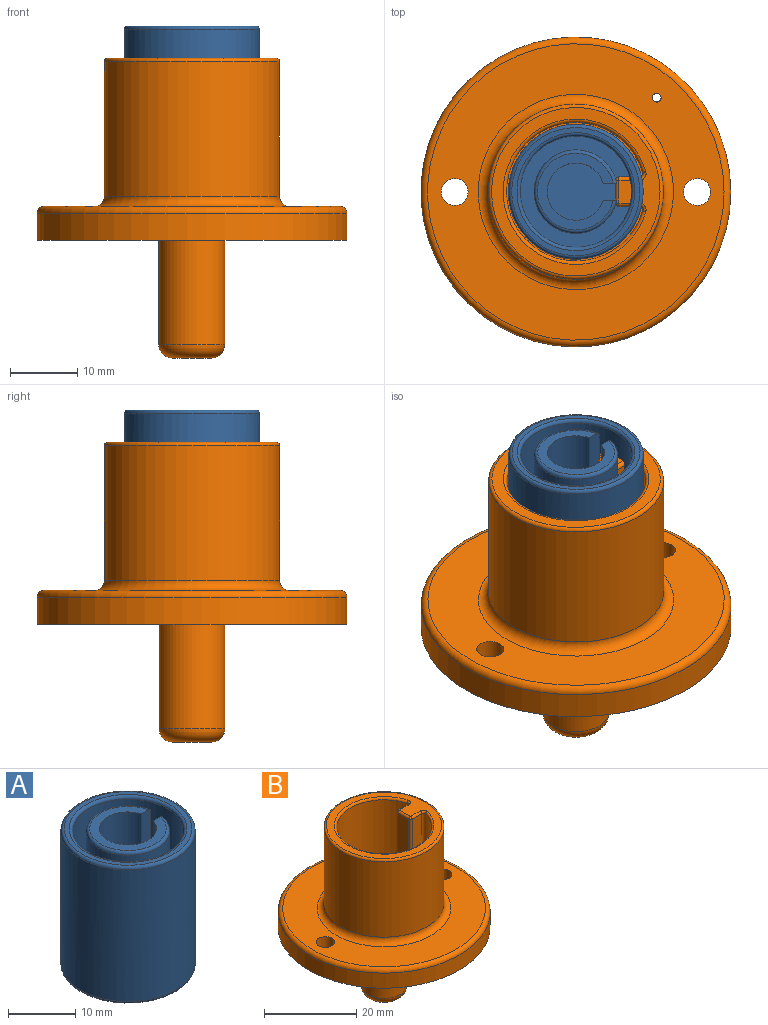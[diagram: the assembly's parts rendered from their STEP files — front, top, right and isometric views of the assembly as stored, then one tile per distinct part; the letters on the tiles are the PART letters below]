
ASSEMBLY  parts=2 mates=1
PART A: 21 faces, bbox 21.6x21.6x25 mm
  f0: cylinder r=10mm len=24mm, axis (0,0,1), area 1411.6mm2, adj f14,f15,f16,f17,f20
  f1: plane 11.4x11.26mm, normal (0,0,1), area 41.7mm2, adj f2,f8,f9,f18
  f2: cylinder r=4.25mm len=8.5mm, axis (0,0,-1), area 181.2mm2, adj f1,f7,f8,f9
  f3: cylinder r=6.2mm len=12.4mm, axis (0,0,-1), area 255.1mm2, adj f7,f8,f9,f18
  f4: plane 19x18.66mm, normal (0,0,-1), area 261.6mm2, adj f10,f11,f12,f14,f15,f16
  f5: plane 19x19mm, normal (0,0,1), area 43mm2, adj f19,f20
  f6: cylinder r=8.25mm len=16.5mm, axis (0,0,1), area 362.9mm2, adj f7,f19
  f7: plane 16.5x16.5mm, normal (0,0,1), area 154.7mm2, adj f2,f3,f6,f8,f9
  f8: plane 7.5x2.01mm, normal (0,-1,0), area 15mm2, adj f1,f2,f3,f7,f18
  f9: plane 7.5x2.01mm, normal (0,1,0), area 15mm2, adj f1,f2,f3,f7,f18
  f10: plane 15x4.01mm, normal (0,1,0), area 60.2mm2, adj f4,f11,f13,f15
  f11: plane 15x5mm, normal (1,0,0), area 75mm2, adj f4,f10,f12,f13
  f12: plane 15x4.01mm, normal (0,-1,0), area 60.2mm2, adj f4,f11,f13,f16
  f13: plane 5.04x4.5mm, normal (0,0,-1), area 21.9mm2, adj f10,f11,f12,f15,f16,f17
  f14: torus R=9.5mm, axis (0,0,1), area 44mm2, adj f0,f4,f15,f16
  f15: cylinder r=0.5mm len=15.5mm, axis (0,0,1), area 14.2mm2, adj f0,f4,f10,f13,f14,f17
  f16: cylinder r=0.5mm len=15.5mm, axis (0,0,1), area 14.2mm2, adj f0,f4,f12,f13,f14,f17
  f17: torus R=9.5mm, axis (0,0,-1), area 4.4mm2, adj f0,f13,f15,f16
  f18: torus R=5.7mm, axis (0,0,1), area 27.7mm2, adj f1,f3,f8,f9
  f19: torus R=8.75mm, axis (0,0,1), area 41.6mm2, adj f5,f6
  f20: torus R=9.5mm, axis (0,0,1), area 48.5mm2, adj f0,f5
PART B: 31 faces, bbox 49.8x49.8x44.5 mm
  f0: cylinder r=10.3mm len=21.5mm, axis (0,0,-1), area 1267.8mm2, adj f1,f20,f24,f26
  f1: plane 20.6x20.22mm, normal (0,0,1), area 314.2mm2, adj f0,f7,f8,f9,f15,f17,f20,f26
  f2: cylinder r=23mm len=46mm, axis (0,0,1), area 578.1mm2, adj f3,f29
  f3: plane 46x46mm, normal (0,0,-1), area 1560mm2, adj f2,f10,f11,f12,f30
  f4: plane 44x44mm, normal (0,0,1), area 833.6mm2, adj f10,f11,f28,f29,f30
  f5: cylinder r=13mm len=26mm, axis (0,0,-1), area 1633.6mm2, adj f27,f28
  f6: plane 25x25mm, normal (0,0,1), area 140mm2, adj f18,f19,f22,f23,f24,f25,f27
  f7: plane 21.5x3.4mm, normal (-1,0,0), area 73.1mm2, adj f1,f15,f17,f18
  f8: plane 21.5x3.02mm, normal (0,-1,0), area 64.9mm2, adj f1,f17,f23,f26
  f9: plane 21.5x3.02mm, normal (0,1,0), area 64.9mm2, adj f1,f15,f19,f20
  f10: cylinder r=2mm len=5mm, axis (0,0,1), area 62.8mm2, adj f3,f4
  f11: cylinder r=2mm len=5mm, axis (0,0,1), area 62.8mm2, adj f3,f4
  f12: cylinder r=4.9mm len=15.5mm, axis (0,0,1), area 477.2mm2, adj f3,f14
  f13: plane 5.8x5.8mm, normal (0,0,-1), area 26.4mm2, adj f14
  f14: torus R=2.9mm, axis (0,0,-1), area 82.4mm2, adj f12,f13
  f15: cylinder r=0.5mm len=21.5mm, axis (0,0,1), area 16.9mm2, adj f1,f7,f9,f16
  f16: sphere r=0.5mm, area 0.4mm2, adj f15,f18,f19
  f17: cylinder r=0.5mm len=21.5mm, axis (0,0,-1), area 16.9mm2, adj f1,f7,f8,f21
  f18: cylinder r=0.5mm len=3.4mm, axis (0,1,0), area 2.7mm2, adj f6,f7,f16,f21
  f19: cylinder r=0.5mm len=3.02mm, axis (1,0,0), area 2.4mm2, adj f6,f9,f16,f22
  f20: cylinder r=0.5mm len=21.5mm, axis (0,0,-1), area 19.9mm2, adj f0,f1,f9,f22
  f21: sphere r=0.5mm, area 0.4mm2, adj f17,f18,f23
  f22: torus R=1mm, axis (0,0,1), area 1mm2, adj f6,f19,f20,f24
  f23: cylinder r=0.5mm len=3.02mm, axis (-1,0,0), area 2.4mm2, adj f6,f8,f21,f25
  f24: torus R=10.8mm, axis (0,0,1), area 47.1mm2, adj f0,f6,f22,f25
  f25: torus R=1mm, axis (0,0,1), area 1mm2, adj f6,f23,f24,f26
  f26: cylinder r=0.5mm len=21.5mm, axis (0,0,-1), area 19.9mm2, adj f0,f1,f8,f25
  f27: torus R=12.5mm, axis (0,0,1), area 63.3mm2, adj f5,f6
  f28: torus R=14.5mm, axis (0,0,1), area 200.5mm2, adj f4,f5
  f29: torus R=22mm, axis (0,0,1), area 223.4mm2, adj f2,f4
  f30: cylinder r=0.65mm len=5mm, axis (0,0,1), area 20.4mm2, adj f3,f4
PLACE A t=(0,0,47.28)mm
PLACE B t=(0,0,20.5)mm
MATE slider B.f0 <-> A.f0  axis (0,0,1) through (0,0,20.5)mm
